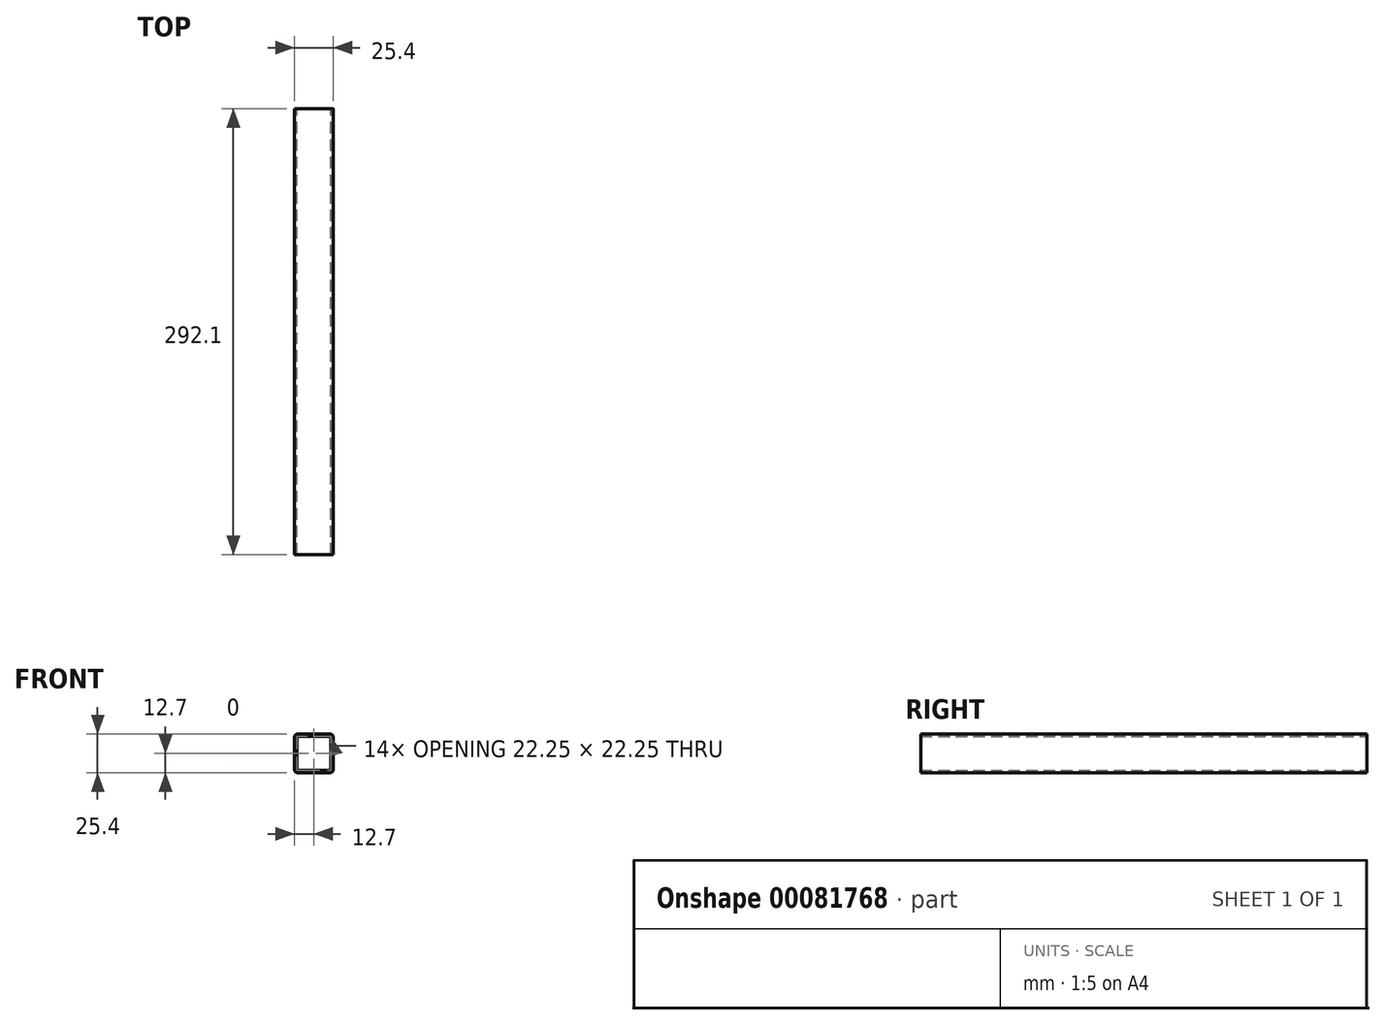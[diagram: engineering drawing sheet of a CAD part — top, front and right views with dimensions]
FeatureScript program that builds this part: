
annotation { "Feature Type Name" : "Feature", "Feature Type Description" : "" }
export const myFeature = defineFeature(function(context is Context, id is Id, definition is map)
    precondition{}
    {
        {
            var Q0;
            Q0=qCreatedBy(makeId("Front.planeOp"),FACE);
            var sketch = newSketch(context, id + "F0", { "sketchPlane" : qUnion([Q0])});
            skLineSegment(sketch, "E0.bottom", {"start": v(-10.62, -12.7) * mm, "end": v(10.62, -12.7) * mm});
            skLineSegment(sketch, "E0.top", {"start": v(-10.62, 12.7) * mm, "end": v(10.62, 12.7) * mm});
            skLineSegment(sketch, "E0.left", {"start": v(-12.7, -10.62) * mm, "end": v(-12.7, 10.62) * mm});
            skLineSegment(sketch, "E0.right", {"start": v(12.7, -10.62) * mm, "end": v(12.7, 10.62) * mm});
            skPoint(sketch, "E0.middle", {"position": v(0, 0) * mm});
            skLineSegment(sketch, "E1.bottom", {"start": v(10.62, -11.13) * mm, "end": v(-10.62, -11.13) * mm});
            skLineSegment(sketch, "E1.top", {"start": v(10.62, 11.13) * mm, "end": v(-10.62, 11.13) * mm});
            skLineSegment(sketch, "E1.left", {"start": v(11.13, -10.62) * mm, "end": v(11.13, 10.62) * mm});
            skLineSegment(sketch, "E1.right", {"start": v(-11.13, -10.62) * mm, "end": v(-11.13, 10.62) * mm});
            skPoint(sketch, "E2.visualSharp", {"position": v(-11.13, 11.13) * mm});
            skArc(sketch, "E2.filletArc", {"start": v(-10.62, 11.13) * mm, "mid": v(-10.98, 10.98) * mm, "end": v(-11.13, 10.62) * mm});
            skPoint(sketch, "E3.visualSharp", {"position": v(11.13, 11.13) * mm});
            skArc(sketch, "E3.filletArc", {"start": v(11.13, 10.62) * mm, "mid": v(10.98, 10.98) * mm, "end": v(10.62, 11.13) * mm});
            skPoint(sketch, "E4.visualSharp", {"position": v(11.13, -11.13) * mm});
            skArc(sketch, "E4.filletArc", {"start": v(10.62, -11.13) * mm, "mid": v(10.98, -10.98) * mm, "end": v(11.13, -10.62) * mm});
            skPoint(sketch, "E5.visualSharp", {"position": v(-11.13, -11.13) * mm});
            skArc(sketch, "E5.filletArc", {"start": v(-11.13, -10.62) * mm, "mid": v(-10.98, -10.98) * mm, "end": v(-10.62, -11.13) * mm});
            skPoint(sketch, "E6.visualSharp", {"position": v(-12.7, 12.7) * mm});
            skArc(sketch, "E6.filletArc", {"start": v(-10.62, 12.7) * mm, "mid": v(-12.09, 12.09) * mm, "end": v(-12.7, 10.62) * mm});
            skPoint(sketch, "E7.visualSharp", {"position": v(12.7, 12.7) * mm});
            skArc(sketch, "E7.filletArc", {"start": v(12.7, 10.62) * mm, "mid": v(12.09, 12.09) * mm, "end": v(10.62, 12.7) * mm});
            skPoint(sketch, "E8.visualSharp", {"position": v(-12.7, -12.7) * mm});
            skArc(sketch, "E8.filletArc", {"start": v(-12.7, -10.62) * mm, "mid": v(-12.09, -12.09) * mm, "end": v(-10.62, -12.7) * mm});
            skPoint(sketch, "E9.visualSharp", {"position": v(12.7, -12.7) * mm});
            skArc(sketch, "E9.filletArc", {"start": v(10.62, -12.7) * mm, "mid": v(12.09, -12.09) * mm, "end": v(12.7, -10.62) * mm});
            skSolve(sketch);
        }
        {
            var Q0;
            Q0=qSketchRegion(id+"F0",true);
            extrude(context, id + "F1", {"entities" : qUnion([Q0]), "depth" : 292.1 * mm});
        }
    });
